# Revit family: Pair_Fade_Table System Final
name_source: partatom
category: Furniture Systems
revit_build: Autodesk Revit 2018 (Build: 20170223_1515(x64)
units: mm (PartAtom-declared; Revit-internal decimal feet)

## family parameters
Always vertical = Yes
Cut with Voids When Loaded = No
Part Type = Normal
Room Calculation Point = No
Round Connector Dimension = Use Diameter
Shared = No
Work Plane-Based = No

## types (15) — shared parameters
2pk = Yes
X = 2
Y = 4
zero-valued in all types: Length

## per-type parameters (varying)
| type | 10pk | 10pk End Panel | 4pk | 4pk End Panel | 6pk | 6pk End Panel | 8pk | 8pk End Panel | Base Length | End Panel Offset | Height | M 48 | M 60 | M 72 |
| 48" Module - 2pk | No | No | No | No | No | No | No | No | 49.122 " | 49.122 " | 29 " | Yes | No | No |
| 60" Module - 2pk | No | No | No | No | No | No | No | No | 61.118 " | 61.118 " | 29 " | No | Yes | No |
| 72" Module - 2pk | No | No | No | No | No | No | No | No | 73.118 " | 73.118 " | 29 " | No | No | Yes |
| 48" Module - 4pk | No | No | Yes | Yes | No | No | No | No | 49.122 " | 98.244 " | 29 " | Yes | No | No |
| 60" Module - 4pk | No | No | Yes | Yes | No | No | No | No | 61.118 " | 122.236 " | 29 " | No | Yes | No |
| 72" Module - 4pk | No | No | Yes | Yes | No | No | No | No | 73.118 " | 146.236 " | 29 " | No | No | Yes |
| 48" Module - 6pk | No | No | Yes | No | Yes | Yes | No | No | 49.122 " | 147.366 " | 29 " | Yes | No | No |
| 60" Module - 6pk | No | No | Yes | No | Yes | Yes | No | No | 61.118 " | 183.354 " | 29 " | No | Yes | No |
| 72" Module - 6pk | No | No | Yes | No | Yes | Yes | No | No | 73.118 " | 219.354 " | 29 " | No | No | Yes |
| 48" Module - 8pk | No | No | Yes | No | Yes | No | Yes | Yes | 49.122 " | 196.488 " | 29 " | Yes | No | No |
| 60" Module - 8pk | No | No | Yes | No | Yes | No | Yes | Yes | 61.118 " | 244.472 " | 29 " | No | Yes | No |
| 72" Module - 8pk | No | No | Yes | No | Yes | No | Yes | Yes | 73.118 " | 292.472 " | 29 " | No | No | Yes |
| 48" Module - 10pk | Yes | Yes | Yes | No | Yes | No | Yes | No | 49.122 " | 245.61 " | 0 " | Yes | No | No |
| 60" Module - 10pk | Yes | Yes | Yes | No | Yes | No | Yes | No | 61.118 " | 305.591 " | 29 " | No | Yes | No |
| 72" Module - 10pk | Yes | Yes | Yes | No | Yes | No | Yes | No | 73.118 " | 365.591 " | 29 " | No | No | Yes |

## geometry (parser evidence)
native form markers: Sweep x23
no freeform markers — native parametric forms only
